# Revit family: 8(10,12,14,16,18)kW
name_source: partatom
category: Mechanical Equipment
revit_build: Autodesk Revit 2013 (Build: 20120221_2030(x64)
units: mm (PartAtom-declared; Revit-internal decimal feet)

## types (6) — shared parameters
Casing color = SB2098
Condensation = Air
Depth = 409 mm  [stored 1.34186 ft]
Gas = R32
Height = 864 mm  [stored 2.83465 ft]
Installation = Outdoor installation
Liquid pipe = 9.5 mm  [stored 0.031168 ft]
Liquid pipe Radius = 4.75 mm  [stored 0.015584 ft]
Manufacturer = Midea
Power supply = 220-240V~ 50Hz
Series = VRF
Width = 1038 mm
clearance access behind = 1000 mm  [stored 3.28084 ft]
clearance access front = 1000 mm  [stored 3.28084 ft]
clearance access left = 1000 mm  [stored 3.28084 ft]
clearance access right = 1000 mm  [stored 3.28084 ft]

## per-type parameters (varying)
| type | Cooling Capacity | Cooling Power Input | Gas pipe | Gas pipe Radius | Heating Capacity | Heating Power Input | Maximum Fuse Amps | Minimum Circuit Amps | Net Weight |
| 8kw | 7.20 kW | 2.00 kW | 15.9 mm  [stored 0.0521654 ft] | 7.95 mm  [stored 0.0260827 ft] | 9.00 kW | 2.50 kW | 25 A | 21 A | 77.00 kg |
| 10kw | 9.00 kW | 2.80 kW | 15.9 mm  [stored 0.0521654 ft] | 7.95 mm  [stored 0.0260827 ft] | 10.80 kW | 3.20 kW | 25 A | 24 A | 77.00 kg |
| 12kw | 12.30 kW | 3.70 kW | 15.9 mm  [stored 0.0521654 ft] | 7.95 mm  [stored 0.0260827 ft] | 14.00 kW | 3.60 kW | 32 A | 32 A | 94.00 kg |
| 14kw | 14.00 kW | 4.70 kW | 15.9 mm  [stored 0.0521654 ft] | 7.95 mm  [stored 0.0260827 ft] | 16.00 kW | 4.20 kW | 40 A | 35 A | 94.00 kg |
| 16kw | 15.50 kW | 5.30 kW | 15.9 mm  [stored 0.0521654 ft] | 7.95 mm  [stored 0.0260827 ft] | 17.50 kW | 4.70 kW | 40 A | 40 A | 94.00 kg |
| 18kW | 17.50 kW | 6.50 kW | 19.1 mm  [stored 0.062664 ft] | 9.55 mm  [stored 0.031332 ft] | 19.50 kW | 5.60 kW | 40 A | 40 A | 94.00 kg |

note: column(s) folded — value = type name in every type: Model

note: [stored X ft] marks values corroborated as IEEE doubles in the binary element streams (Revit-internal decimal feet)

## geometry (parser evidence)
native form markers: Sweep x16
no freeform markers — native parametric forms only
